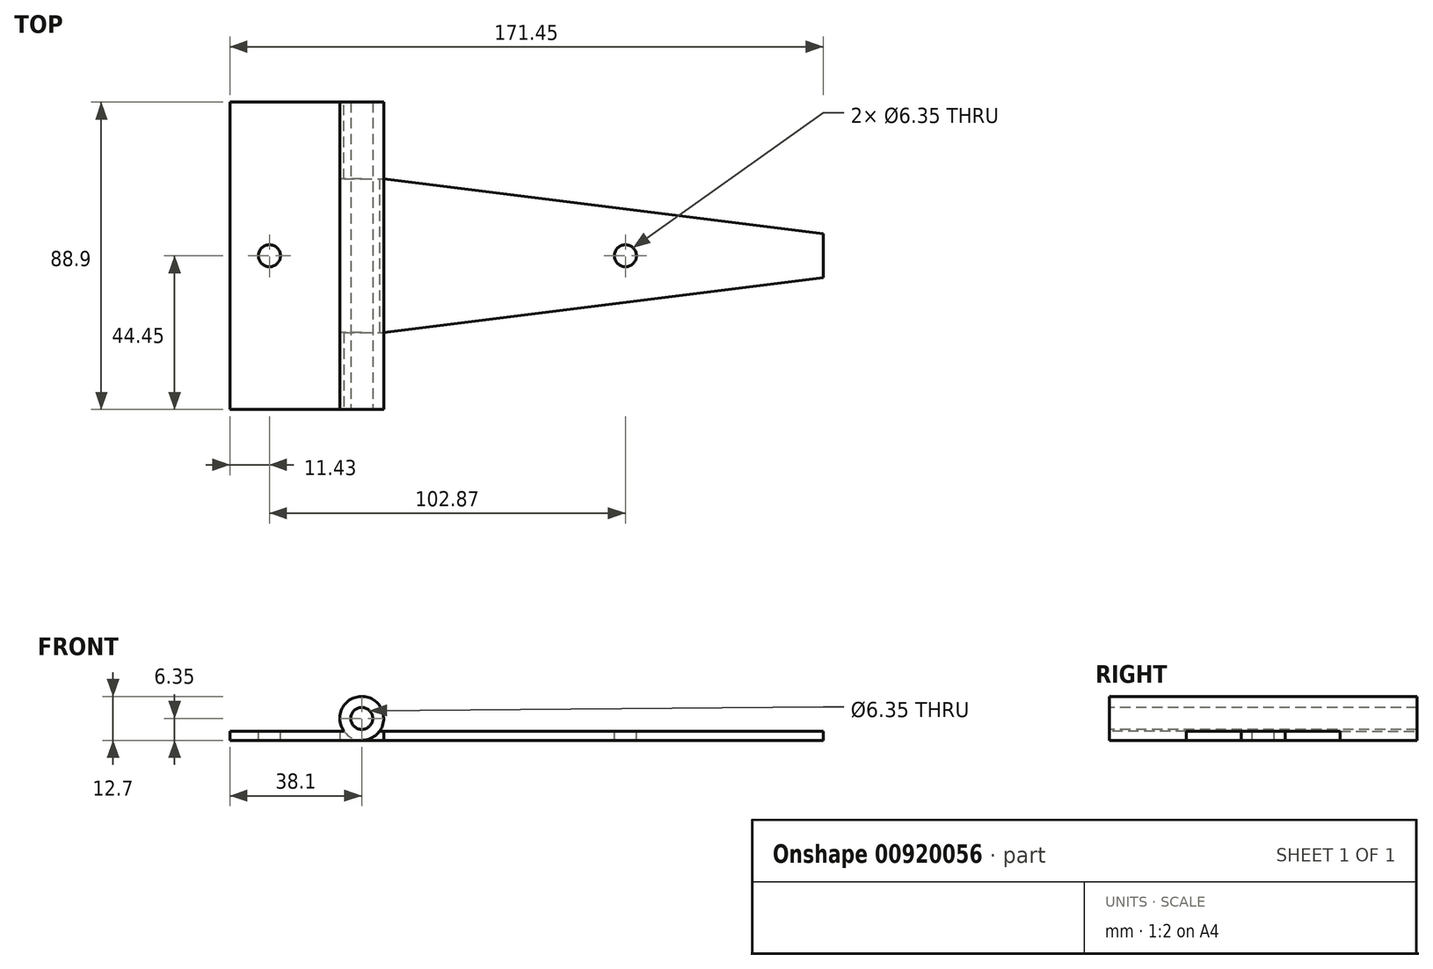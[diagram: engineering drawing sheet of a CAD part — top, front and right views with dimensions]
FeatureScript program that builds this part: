
annotation { "Feature Type Name" : "Feature", "Feature Type Description" : "" }
export const myFeature = defineFeature(function(context is Context, id is Id, definition is map)
    precondition{}
    {
        {
            var Q0;
            Q0=qCreatedBy(makeId("Top.planeOp"),FACE);
            var sketch = newSketch(context, id + "F0", { "sketchPlane" : qUnion([Q0])});
            skLineSegment(sketch, "E0", {"start": v(0, 22.22) * mm, "end": v(0, -22.22) * mm});
            skLineSegment(sketch, "E1", {"start": v(127, 6.35) * mm, "end": v(0, 22.22) * mm});
            skLineSegment(sketch, "E2", {"start": v(0, -22.23) * mm, "end": v(127, -6.35) * mm});
            skLineSegment(sketch, "E3", {"start": v(127, -6.35) * mm, "end": v(127, 6.35) * mm});
            skSolve(sketch);
        }
        {
            var Q0;
            Q0=makeQuery(id+"F0.imprint","IMPRINT",FACE,{"disambiguationData":[TD([[makeQuery(id+"F0.imprint","IMPRINT",EDGE,{"derivedFrom":sQuery(id+"F0.wireOp",EDGE,"E0")}),1.0]])]});
            extrude(context, id + "F1", {"entities" : qUnion([Q0]), "depth" : 2.67 * mm, "offsetDistance" : 25.4 * mm});
        }
        {
            var Q0;
            Q0=makeQuery(id+"F1.opExtrude","SWEPT_FACE",FACE,{"disambiguationData":[OSD([sQuery(id+"F0.wireOp",EDGE,"E0")])]});
            extrude(context, id + "F2", {"entities" : qUnion([Q0]), "operationType" : NewBodyOperationType.ADD, "depth" : 6.35 * mm, "offsetDistance" : 25.4 * mm});
        }
        {
            var Q0;
            Q0=makeQuery(id+"F2.opExtrude","SWEPT_FACE",FACE,{"disambiguationData":[OSD([sQuery(id+"F0.wireOp",EDGE,"E0"),sQuery(id+"F0.wireOp",EDGE,"E2")])]});
            var sketch = newSketch(context, id + "F3", { "sketchPlane" : qUnion([Q0])});
            skCircle(sketch, "E4", {"center": v(-6.35, 6.35) * mm, "radius": 6.35 * mm});
            skSolve(sketch);
        }
        {
            var Q0;
            {var subQ1=sQuery(id+"F0.wireOp",EDGE,"E2");var subQ2=sQuery(id+"F0.wireOp",EDGE,"E0");var subQ3=makeQuery(id+"F2.opExtrude","CAP_EDGE",EDGE,{"disambiguationData":[OSD([subQ2,subQ1])],"isStart":false});Q0=makeQuery(id+"F3.imprint","IMPRINT",FACE,{"disambiguationData":[TD([[makeQuery(id+"F3.imprint","IMPRINT",EDGE,{"derivedFrom":subQ3}),-1.0]])]});}
            var Q1;
            Q1=makeQuery(id+"F2.opExtrude","SWEPT_FACE",FACE,{"disambiguationData":[OSD([sQuery(id+"F0.wireOp",EDGE,"E0"),sQuery(id+"F0.wireOp",EDGE,"E1")])]});
            extrude(context, id + "F4", {"entities" : qUnion([Q0]), "operationType" : NewBodyOperationType.ADD, "endBound" : BoundingType.UP_TO_SURFACE, "oppositeDirection" : true, "depth" : 25.4 * mm, "endBoundEntityFace" : qUnion([Q1]), "offsetDistance" : 25.4 * mm});
        }
        {
            var Q0;
            {var subQ0=sQuery(id+"F0.wireOp",EDGE,"E2");var subQ1=sQuery(id+"F0.wireOp",EDGE,"E0");Q0=makeQuery(id+"F4.boolean.opBoolean","MERGE",FACE,{"derivedFrom":[makeQuery(id+"F2.opExtrude","SWEPT_FACE",FACE,{"disambiguationData":[OSD([subQ1,subQ0])]}),makeQuery(id+"F4.opExtrude","CAP_FACE",FACE,{"disambiguationData":[OSD([subQ1,subQ0,sQuery(id+"F3.wireOp",EDGE,"E4")])],"isStart":true})]});}
            var sketch = newSketch(context, id + "F5", { "sketchPlane" : qUnion([Q0])});
            skCircle(sketch, "E5", {"center": v(-6.35, 6.35) * mm, "radius": 3.18 * mm});
            skSolve(sketch);
        }
        {
            var Q0;
            Q0=makeQuery(id+"F5.imprint","IMPRINT",FACE,{"disambiguationData":[TD([[makeQuery(id+"F5.imprint","IMPRINT",EDGE,{"derivedFrom":sQuery(id+"F5.wireOp",EDGE,"E5")}),1.0]])]});
            var Q1;
            {var subQ0=sQuery(id+"F0.wireOp",EDGE,"E0");Q1=makeQuery(id+"F4.boolean.opBoolean","MERGE",FACE,{"derivedFrom":[makeQuery(id+"F2.opExtrude","SWEPT_FACE",FACE,{"disambiguationData":[OSD([subQ0,sQuery(id+"F0.wireOp",EDGE,"E1")])]}),makeQuery(id+"F4.opExtrude","CAP_FACE",FACE,{"disambiguationData":[OSD([subQ0,sQuery(id+"F0.wireOp",EDGE,"E2"),sQuery(id+"F3.wireOp",EDGE,"E4")])],"isStart":false})]});}
            extrude(context, id + "F6", {"entities" : qUnion([Q0]), "operationType" : NewBodyOperationType.REMOVE, "endBound" : BoundingType.UP_TO_SURFACE, "oppositeDirection" : true, "depth" : 25.4 * mm, "endBoundEntityFace" : qUnion([Q1]), "offsetDistance" : 25.4 * mm});
        }
        {
            var Q0;
            Q0=qCreatedBy(makeId("Top.planeOp"),FACE);
            var sketch = newSketch(context, id + "F7", { "sketchPlane" : qUnion([Q0])});
            skLineSegment(sketch, "E6", {"start": v(-12.7, -38.1) * mm, "end": v(-12.7, 38.1) * mm});
            skLineSegment(sketch, "E7.bottom", {"start": v(-12.7, 44.45) * mm, "end": v(-44.45, 44.45) * mm});
            skLineSegment(sketch, "E7.top", {"start": v(-12.7, -44.45) * mm, "end": v(-44.45, -44.45) * mm});
            skLineSegment(sketch, "E7.left", {"start": v(-12.7, 44.45) * mm, "end": v(-12.7, -44.45) * mm});
            skLineSegment(sketch, "E7.right", {"start": v(-44.45, 44.45) * mm, "end": v(-44.45, -44.45) * mm});
            skLineSegment(sketch, "E8.0", {"start": v(127, -6.35) * mm, "end": v(127, 6.35) * mm, "construction": true});
            skSolve(sketch);
        }
        {
            var Q0;
            {var subQ0=sQuery(id+"F7.wireOp",EDGE,"E7.bottom");Q0=makeQuery(id+"F7.imprint","IMPRINT",FACE,{"disambiguationData":[TD([[makeQuery(id+"F7.imprint","IMPRINT",EDGE,{"derivedFrom":subQ0}),1.0]])]});}
            extrude(context, id + "F8", {"entities" : qUnion([Q0]), "depth" : 2.67 * mm, "offsetDistance" : 25.4 * mm});
        }
        {
            var Q0;
            Q0=makeQuery(id+"F8.opExtrude","SWEPT_FACE",FACE,{"disambiguationData":[OSD([sQuery(id+"F7.wireOp",EDGE,"E7.left")])]});
            var sketch = newSketch(context, id + "F9", { "sketchPlane" : qUnion([Q0])});
            skLineSegment(sketch, "E9.0", {"start": v(-22.23, 2.67) * mm, "end": v(-22.23, 0) * mm});
            skLineSegment(sketch, "E10.0", {"start": v(-44.45, 2.67) * mm, "end": v(-44.45, 0) * mm});
            skLineSegment(sketch, "E11", {"start": v(-44.45, 2.67) * mm, "end": v(-22.23, 2.67) * mm});
            skLineSegment(sketch, "E12", {"start": v(-22.23, 0) * mm, "end": v(-44.45, 0) * mm});
            skLineSegment(sketch, "E13.0", {"start": v(22.22, 2.67) * mm, "end": v(22.22, 0) * mm});
            skLineSegment(sketch, "E14.0", {"start": v(44.45, 2.67) * mm, "end": v(44.45, 0) * mm});
            skLineSegment(sketch, "E15", {"start": v(22.22, 2.67) * mm, "end": v(44.45, 2.67) * mm});
            skLineSegment(sketch, "E16", {"start": v(44.45, 0) * mm, "end": v(22.22, 0) * mm});
            skSolve(sketch);
        }
        {
            var Q0;
            Q0=makeQuery(id+"F9.imprint","IMPRINT",FACE,{"disambiguationData":[TD([[makeQuery(id+"F9.imprint","IMPRINT",EDGE,{"derivedFrom":sQuery(id+"F9.wireOp",EDGE,"E9.0")}),-1.0]])]});
            var Q1;
            Q1=makeQuery(id+"F9.imprint","IMPRINT",FACE,{"disambiguationData":[TD([[makeQuery(id+"F9.imprint","IMPRINT",EDGE,{"derivedFrom":sQuery(id+"F9.wireOp",EDGE,"E13.0")}),1.0]])]});
            extrude(context, id + "F10", {"entities" : qUnion([Q0, Q1]), "operationType" : NewBodyOperationType.ADD, "depth" : 6.35 * mm, "offsetDistance" : 25.4 * mm});
        }
        {
            var Q0;
            Q0=makeQuery(id+"F10.boolean.opBoolean","MERGE",FACE,{"derivedFrom":[makeQuery(id+"F8.opExtrude","SWEPT_FACE",FACE,{"disambiguationData":[OSD([sQuery(id+"F7.wireOp",EDGE,"E7.top")])]}),makeQuery(id+"F10.opExtrude","SWEPT_FACE",FACE,{"disambiguationData":[OSD([sQuery(id+"F9.wireOp",EDGE,"E10.0")])]})]});
            var sketch = newSketch(context, id + "F11", { "sketchPlane" : qUnion([Q0])});
            skCircle(sketch, "E17.0", {"center": v(-6.35, 6.35) * mm, "radius": 3.18 * mm});
            skCircle(sketch, "E18", {"center": v(-6.35, 6.35) * mm, "radius": 6.35 * mm});
            skSolve(sketch);
        }
        {
            var Q0;
            Q0=makeQuery(id+"F11.imprint","IMPRINT",FACE,{"disambiguationData":[TD([[makeQuery(id+"F11.imprint","IMPRINT",EDGE,{"derivedFrom":sQuery(id+"F11.wireOp",EDGE,"E17.0")}),-1.0]])]});
            var Q1;
            {var subQ0=sQuery(id+"F0.wireOp",EDGE,"E2");var subQ1=sQuery(id+"F0.wireOp",EDGE,"E0");Q1=makeQuery(id+"F4.boolean.opBoolean","MERGE",FACE,{"derivedFrom":[makeQuery(id+"F2.opExtrude","SWEPT_FACE",FACE,{"disambiguationData":[OSD([subQ1,subQ0])]}),makeQuery(id+"F4.opExtrude","CAP_FACE",FACE,{"disambiguationData":[OSD([subQ1,subQ0,sQuery(id+"F3.wireOp",EDGE,"E4")])],"isStart":true})]});}
            extrude(context, id + "F12", {"entities" : qUnion([Q0]), "operationType" : NewBodyOperationType.ADD, "endBound" : BoundingType.UP_TO_SURFACE, "oppositeDirection" : true, "depth" : 25.4 * mm, "endBoundEntityFace" : qUnion([Q1]), "offsetDistance" : 25.4 * mm});
        }
        {
            var Q0;
            Q0=makeQuery(id+"F10.boolean.opBoolean","MERGE",FACE,{"derivedFrom":[makeQuery(id+"F8.opExtrude","SWEPT_FACE",FACE,{"disambiguationData":[OSD([sQuery(id+"F7.wireOp",EDGE,"E7.bottom")])]}),makeQuery(id+"F10.opExtrude","SWEPT_FACE",FACE,{"disambiguationData":[OSD([sQuery(id+"F9.wireOp",EDGE,"E14.0")])]})]});
            var sketch = newSketch(context, id + "F13", { "sketchPlane" : qUnion([Q0])});
            skCircle(sketch, "E19.0", {"center": v(6.35, 6.35) * mm, "radius": 3.18 * mm});
            skCircle(sketch, "E20", {"center": v(6.35, 6.35) * mm, "radius": 6.35 * mm});
            skSolve(sketch);
        }
        {
            var Q0;
            Q0=makeQuery(id+"F13.imprint","IMPRINT",FACE,{"disambiguationData":[TD([[makeQuery(id+"F13.imprint","IMPRINT",EDGE,{"derivedFrom":sQuery(id+"F13.wireOp",EDGE,"E19.0")}),-1.0]])]});
            var Q1;
            {var subQ0=sQuery(id+"F0.wireOp",EDGE,"E0");Q1=makeQuery(id+"F4.boolean.opBoolean","MERGE",FACE,{"derivedFrom":[makeQuery(id+"F2.opExtrude","SWEPT_FACE",FACE,{"disambiguationData":[OSD([subQ0,sQuery(id+"F0.wireOp",EDGE,"E1")])]}),makeQuery(id+"F4.opExtrude","CAP_FACE",FACE,{"disambiguationData":[OSD([subQ0,sQuery(id+"F0.wireOp",EDGE,"E2"),sQuery(id+"F3.wireOp",EDGE,"E4")])],"isStart":false})]});}
            extrude(context, id + "F14", {"entities" : qUnion([Q0]), "operationType" : NewBodyOperationType.ADD, "endBound" : BoundingType.UP_TO_SURFACE, "oppositeDirection" : true, "depth" : 25.4 * mm, "endBoundEntityFace" : qUnion([Q1]), "offsetDistance" : 25.4 * mm});
        }
        {
            var Q0;
            Q0=makeQuery(id+"F10.boolean.opBoolean","MERGE",FACE,{"derivedFrom":[makeQuery(id+"F8.opExtrude","CAP_FACE",FACE,{"disambiguationData":[OSD([sQuery(id+"F7.wireOp",EDGE,"E7.bottom"),sQuery(id+"F7.wireOp",EDGE,"E7.top"),sQuery(id+"F7.wireOp",EDGE,"E7.left"),sQuery(id+"F7.wireOp",EDGE,"E7.right")])],"isStart":false}),makeQuery(id+"F10.opExtrude","SWEPT_FACE",FACE,{"disambiguationData":[OSD([sQuery(id+"F9.wireOp",EDGE,"E11")])]}),makeQuery(id+"F10.opExtrude","SWEPT_FACE",FACE,{"disambiguationData":[OSD([sQuery(id+"F9.wireOp",EDGE,"E15")])]})]});
            var sketch = newSketch(context, id + "F15", { "sketchPlane" : qUnion([Q0])});
            skCircle(sketch, "E21", {"center": v(-33.02, 0) * mm, "radius": 3.18 * mm});
            skSolve(sketch);
        }
        {
            var Q0;
            Q0=makeQuery(id+"F15.imprint","IMPRINT",FACE,{"disambiguationData":[TD([[makeQuery(id+"F15.imprint","IMPRINT",EDGE,{"derivedFrom":sQuery(id+"F15.wireOp",EDGE,"E21")}),1.0]])]});
            extrude(context, id + "F16", {"entities" : qUnion([Q0]), "operationType" : NewBodyOperationType.REMOVE, "oppositeDirection" : true, "depth" : 25.4 * mm, "offsetDistance" : 25.4 * mm});
        }
        {
            var Q0;
            {var subQ0=sQuery(id+"F0.wireOp",EDGE,"E0");Q0=makeQuery(id+"F2.boolean.opBoolean","MERGE",FACE,{"derivedFrom":[makeQuery(id+"F1.opExtrude","CAP_FACE",FACE,{"disambiguationData":[OSD([subQ0,sQuery(id+"F0.wireOp",EDGE,"E1"),sQuery(id+"F0.wireOp",EDGE,"E2"),sQuery(id+"F0.wireOp",EDGE,"E3")])],"isStart":false}),makeQuery(id+"F2.opExtrude","SWEPT_FACE",FACE,{"disambiguationData":[OSD([subQ0]),TDD([makeQuery(id+"F1.opExtrude","CAP_EDGE",EDGE,{"disambiguationData":[OSD([subQ0])],"isStart":false})])]})]});}
            var sketch = newSketch(context, id + "F17", { "sketchPlane" : qUnion([Q0])});
            skCircle(sketch, "E22", {"center": v(69.85, 0) * mm, "radius": 3.18 * mm});
            skSolve(sketch);
        }
        {
            var Q0;
            Q0=makeQuery(id+"F17.imprint","IMPRINT",FACE,{"disambiguationData":[TD([[makeQuery(id+"F17.imprint","IMPRINT",EDGE,{"derivedFrom":sQuery(id+"F17.wireOp",EDGE,"E22")}),1.0]])]});
            extrude(context, id + "F18", {"entities" : qUnion([Q0]), "operationType" : NewBodyOperationType.REMOVE, "oppositeDirection" : true, "depth" : 25.4 * mm, "offsetDistance" : 25.4 * mm});
        }
    });
